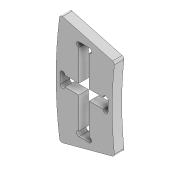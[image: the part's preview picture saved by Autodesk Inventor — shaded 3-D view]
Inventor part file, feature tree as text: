
AUTODESK INVENTOR PART (.ipt)
format: ipt  version: 2020 (Build 240168000, 168)  size: 141,312 bytes
history: native  units: mm
features: extrude x1, fillet x1, sketch x1
ambient origin geometry x8: Origin, YZ Plane, XZ Plane, XY Plane, X Axis, Y Axis, Z Axis, Center Point
bodies: Solid1 (feature_tree)
feature tree (3):
  extrude  "Extrusion1"  Depth=1.75mm
  fillet  "Fillet1"  [1 undecoded]
  sketch  "Sketch1"  dims[d1=6.5mm d3=1.75mm d10=0.0mm d11=0.0mm d31=7.0mm d32=0.0mm d33=1.75mm d43=0.0mm d46=7.5mm d47=1.75mm d48=1.75mm d49=7.5mm d50=7.5mm d51=60.0mm d52=35.0mm d55=3.0mm d57=585.0mm d58=3.0mm d61=15.0deg]
note: 1 required parameter value undecoded (feature->parameter linkage not recoverable at this tier; creation-order binding heuristic only, values carry confidence <= 0.55)
